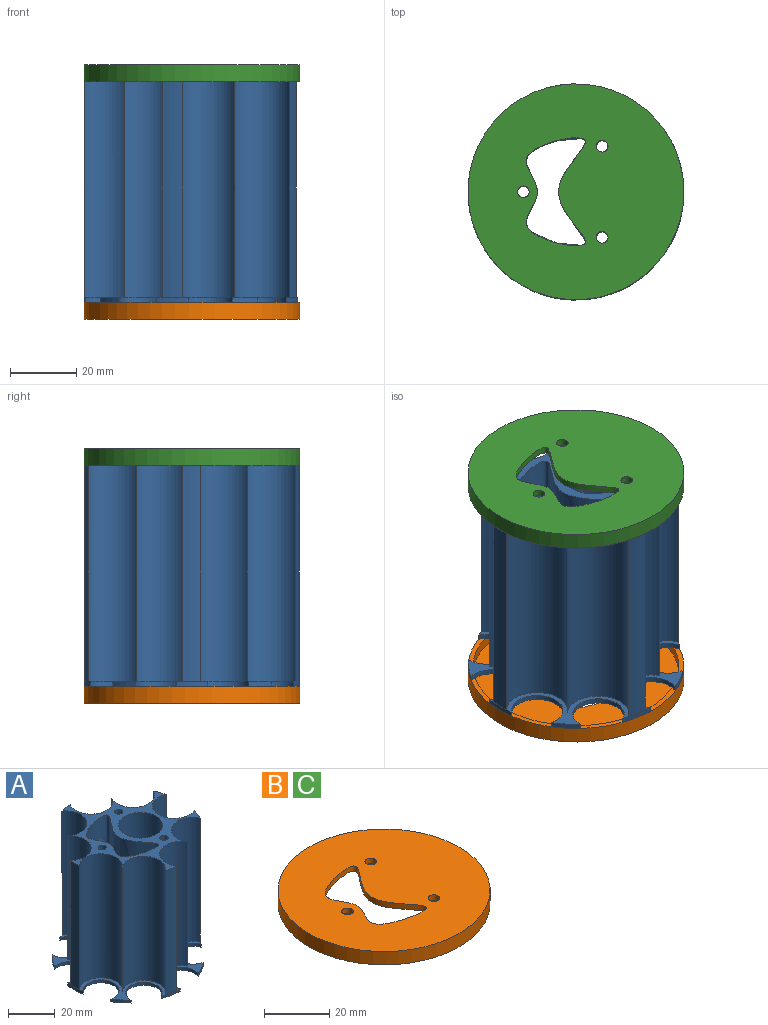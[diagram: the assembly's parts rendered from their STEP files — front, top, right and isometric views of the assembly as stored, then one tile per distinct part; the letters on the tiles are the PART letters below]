
ASSEMBLY  parts=3 mates=4
PART A: 54 faces, bbox 67.9x68.5x70 mm
  f0: plane 38.21x13.53mm, normal (0,0,-1), area 1mm2, adj f22,f51
  f1: plane 18.99x10mm, normal (0,0,-1), area 0.6mm2, adj f18,f50
  f2: plane 3.5x1.77mm, normal (0,0,-1), area 0.1mm2, adj f19,f49
  f3: plane 3.5x1.77mm, normal (0,0,-1), area 0.1mm2, adj f21,f30
  f4: plane 3.5x1.77mm, normal (0,0,-1), area 0.1mm2, adj f20,f29
  f5: cylinder r=9.25mm len=65mm, axis (0,0,-1), area 1926mm2, adj f6,f23,f24,f28
  f6: cylinder r=32.5mm len=65mm, axis (0,0,-1), area 393.9mm2, adj f5,f7,f24,f28
  f7: cylinder r=9.25mm len=65mm, axis (0,0,-1), area 2371.7mm2, adj f6,f8,f24,f28
  f8: cylinder r=32.5mm len=65mm, axis (0,0,-1), area 393.9mm2, adj f7,f9,f24,f28
  f9: cylinder r=9.25mm len=65mm, axis (0,0,-1), area 1926mm2, adj f8,f10,f24,f28
  f10: cylinder r=9.25mm len=65mm, axis (0,0,-1), area 1926mm2, adj f9,f11,f24,f28
  f11: cylinder r=32.5mm len=65mm, axis (0,0,-1), area 393.9mm2, adj f10,f12,f24,f40
  f12: cylinder r=9.25mm len=65mm, axis (0,0,-1), area 1926mm2, adj f11,f13,f24,f27
  f13: cylinder r=9.25mm len=65mm, axis (0,0,-1), area 1926mm2, adj f12,f14,f24,f25,f27
  f14: cylinder r=32.5mm len=65mm, axis (0,0,-1), area 354.9mm2, adj f13,f15,f24,f25
  f15: cylinder r=9.25mm len=65mm, axis (0,0,-1), area 1926mm2, adj f14,f16,f24,f25,f26
  f16: cylinder r=9.25mm len=65mm, axis (0,0,-1), area 1926mm2, adj f15,f17,f24,f26
  f17: cylinder r=32.5mm len=65mm, axis (0,0,-1), area 393.9mm2, adj f16,f23,f24,f32
  f18: cylinder r=9.5mm len=66.5mm, axis (0,0,-1), area 3924.7mm2, adj f1,f24,f50,f53
  f19: cylinder r=1.75mm len=66.5mm, axis (0,0,-1), area 723mm2, adj f2,f24,f49,f53
  f20: cylinder r=1.75mm len=66.5mm, axis (0,0,-1), area 723mm2, adj f4,f24,f29,f53
  f21: cylinder r=1.75mm len=66.5mm, axis (0,0,-1), area 723mm2, adj f3,f24,f30,f53
  f22: extruded ~65x32.54mm, area 6262.5mm2, adj f0,f24,f31,f51
  f23: cylinder r=9.25mm len=65mm, axis (0,0,-1), area 1926mm2, adj f5,f17,f24,f28
  f24: plane 64.73x63.88mm, normal (0,0,1), area 701mm2, adj f5,f6,f7,f8,f9,f10,f11,f12
  f25: plane 5.45x0.15mm, normal (0,0,-1), area 0.2mm2, adj f13,f14,f15,f36
  f26: plane 31.04x27.27mm, normal (0,0,1), area 113.1mm2, adj f15,f16,f32,f33,f34,f35,f36
  f27: plane 31x27.32mm, normal (0,0,1), area 113.1mm2, adj f12,f13,f36,f37,f38,f39,f40
  f28: plane 64.98x36.33mm, normal (0,0,1), area 281.9mm2, adj f5,f6,f7,f8,f9,f10,f23,f32
  f29: cylinder r=1.75mm len=3.5mm, axis (0,0,1), area 8.3mm2, adj f4,f20,f53
  f30: cylinder r=1.75mm len=3.5mm, axis (0,0,1), area 8.3mm2, adj f3,f21,f53
  f31: extruded ~32.54x14.96mm, area 82.6mm2, adj f22,f51,f53
  f32: cylinder r=32.5mm len=9.81mm, axis (0,0,1), area 15mm2, adj f17,f26,f28,f33,f52,f53
  f33: cylinder r=7.75mm len=15.5mm, axis (0,0,1), area 49.4mm2, adj f26,f32,f34,f53
  f34: cylinder r=32.5mm len=6.77mm, axis (0,0,1), area 13.2mm2, adj f26,f33,f35,f53
  f35: cylinder r=7.75mm len=15.5mm, axis (0,0,1), area 49.4mm2, adj f26,f34,f36,f53
  f36: cylinder r=32.5mm len=9.38mm, axis (0,0,1), area 14.1mm2, adj f25,f26,f27,f35,f37,f53
  f37: cylinder r=7.75mm len=15.5mm, axis (0,0,1), area 49.4mm2, adj f27,f36,f38,f53
  f38: cylinder r=32.5mm len=6.79mm, axis (0,0,1), area 13.2mm2, adj f27,f37,f39,f53
  f39: cylinder r=7.75mm len=15.5mm, axis (0,0,1), area 49.4mm2, adj f27,f38,f40,f53
  f40: cylinder r=32.5mm len=9.8mm, axis (0,0,1), area 15mm2, adj f11,f27,f28,f39,f41,f53
  f41: cylinder r=7.75mm len=15.5mm, axis (0,0,1), area 49.4mm2, adj f28,f40,f42,f53
  f42: cylinder r=32.5mm len=7.65mm, axis (0,0,1), area 13.2mm2, adj f28,f41,f43,f53
  f43: cylinder r=7.75mm len=15.4mm, axis (0,0,1), area 49.4mm2, adj f28,f42,f44,f53
  f44: cylinder r=32.5mm len=9.33mm, axis (0,0,1), area 15mm2, adj f28,f43,f45,f53
  f45: cylinder r=7.75mm len=15.5mm, axis (0,0,1), area 49.4mm2, adj f28,f44,f46,f53
  f46: cylinder r=32.5mm len=9.34mm, axis (0,0,1), area 15mm2, adj f28,f45,f47,f53
  f47: cylinder r=7.75mm len=15.4mm, axis (0,0,1), area 49.4mm2, adj f28,f46,f48,f53
  f48: cylinder r=32.5mm len=7.64mm, axis (0,0,1), area 13.2mm2, adj f28,f47,f52,f53
  f49: cylinder r=1.75mm len=3.5mm, axis (0,0,1), area 8.3mm2, adj f2,f19,f53
  f50: cylinder r=9.5mm len=18.99mm, axis (0,0,1), area 44.8mm2, adj f1,f18,f53
  f51: extruded ~32.54x8.03mm, area 62.3mm2, adj f0,f22,f31,f53
  f52: cylinder r=7.75mm len=15.5mm, axis (0,0,1), area 49.4mm2, adj f28,f32,f48,f53
  f53: plane 64.97x64.33mm, normal (0,0,-1), area 1206.7mm2, adj f18,f19,f20,f21,f29,f30,f31,f32
PART B: 9 faces, bbox 65x65x5 mm
  f0: plane 62x62mm, normal (0,0,-1), area 2636.6mm2, adj f1,f2,f3,f4,f7
  f1: cylinder r=1.75mm len=3.5mm, axis (0,0,-1), area 22mm2, adj f0,f6
  f2: cylinder r=1.75mm len=3.5mm, axis (0,0,-1), area 22mm2, adj f0,f6
  f3: cylinder r=1.75mm len=3.5mm, axis (0,0,-1), area 22mm2, adj f0,f6
  f4: extruded ~32.54x17.71mm, area 192.7mm2, adj f0,f6
  f5: cylinder r=32.5mm len=65mm, axis (0,0,-1), area 1021mm2, adj f6,f8
  f6: plane 65x65mm, normal (0,0,1), area 2935.9mm2, adj f1,f2,f3,f4,f5
  f7: cylinder r=31mm len=62mm, axis (0,0,1), area 584.3mm2, adj f0,f8
  f8: plane 65x65mm, normal (0,0,-1), area 299.2mm2, adj f5,f7
PART C: same geometry as B
PLACE A t=(21.58,61.13,-30.47)mm
PLACE B rot(axis=(1,0,0),180deg) t=(21.58,61.13,-34.97)mm
PLACE C t=(21.55,61.13,37.53)mm
MATE fastened B.f5 <-> A.f32  axis (0,0,1) through (21.61,61.13,-31.97)mm
MATE fastened A.f24 <-> C.f5  axis (0,0,1) through (-10.81,58.45,34.53)mm
MATE fastened A.f6 <-> C.f5  axis (0,0,1) through (21.58,61.13,34.53)mm
MATE fastened B.f5 <-> A.f32  axis (0,0,1) through (21.61,61.13,-31.97)mm
